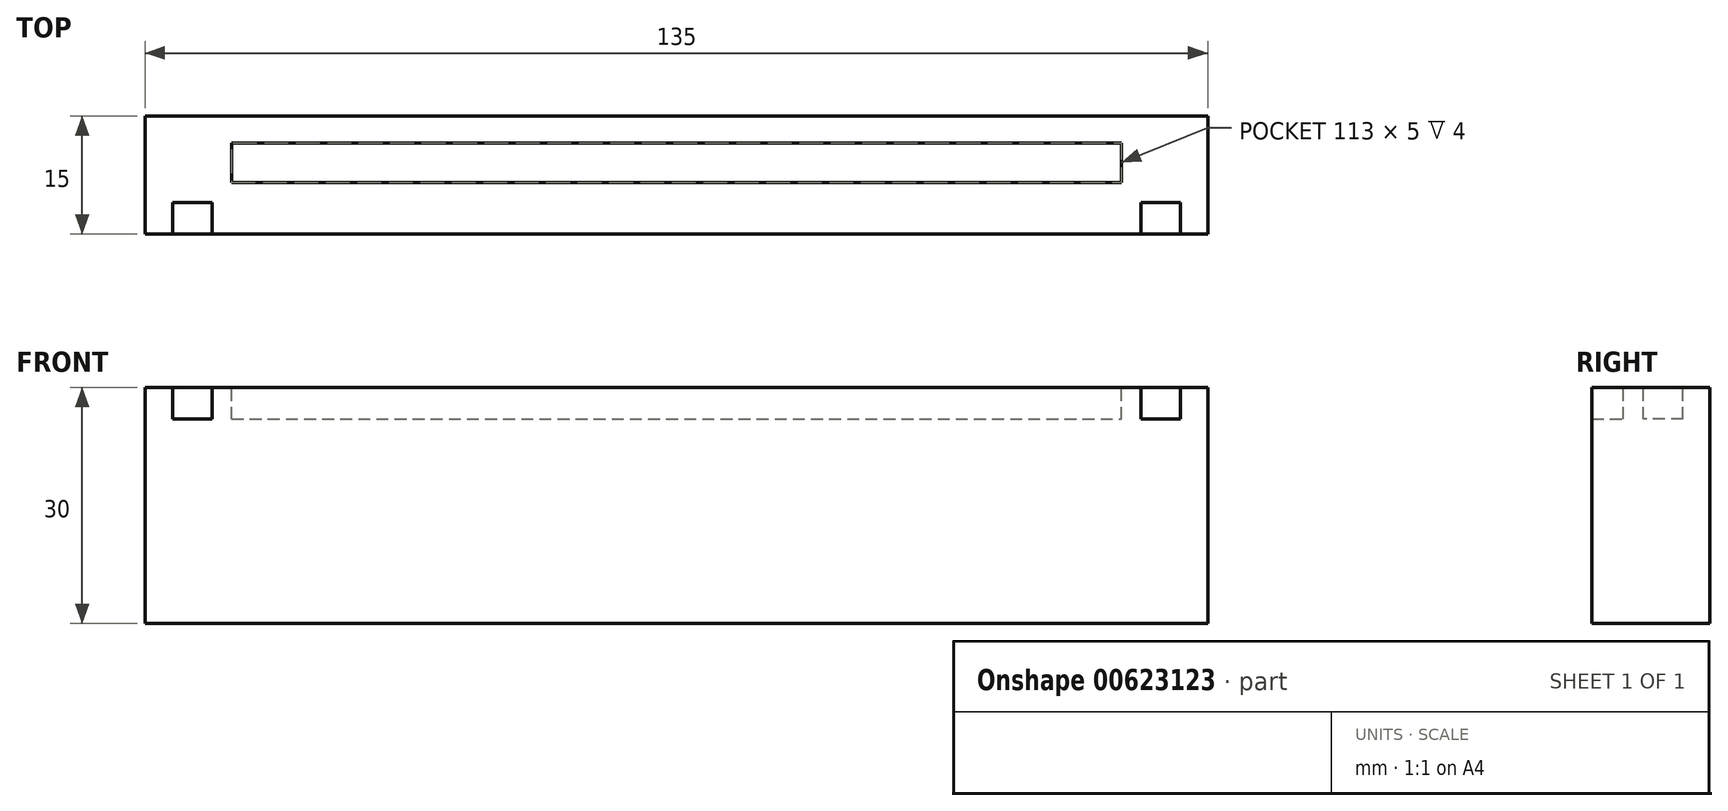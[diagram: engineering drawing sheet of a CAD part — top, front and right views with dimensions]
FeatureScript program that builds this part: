
annotation { "Feature Type Name" : "Feature", "Feature Type Description" : "" }
export const myFeature = defineFeature(function(context is Context, id is Id, definition is map)
    precondition{}
    {
        {
            var Q0;
            Q0=qCreatedBy(makeId("Front.planeOp"),FACE);
            var sketch = newSketch(context, id + "F0", { "sketchPlane" : qUnion([Q0])});
            skLineSegment(sketch, "E0.bottom", {"start": v(-67.5, 0) * mm, "end": v(67.5, 0) * mm});
            skLineSegment(sketch, "E0.top", {"start": v(-67.5, 30) * mm, "end": v(67.5, 30) * mm});
            skLineSegment(sketch, "E0.left", {"start": v(-67.5, 0) * mm, "end": v(-67.5, 30) * mm});
            skLineSegment(sketch, "E0.right", {"start": v(67.5, 0) * mm, "end": v(67.5, 30) * mm});
            skSolve(sketch);
        }
        {
            var Q0;
            Q0 = qSketchRegion(id + "F0", true);
            extrude(context, id + "F1", {"entities" : qUnion([Q0]), "depth" : 15 * mm, "offsetDistance" : 25 * mm});
        }
        {
            var Q0;
            Q0=makeQuery(id+"F1.opExtrude","SWEPT_FACE",FACE,{"disambiguationData":[OSD([sQuery(id+"F0.wireOp",EDGE,"E0.top")])]});
            var sketch = newSketch(context, id + "F2", { "sketchPlane" : qUnion([Q0])});
            skLineSegment(sketch, "E1.bottom", {"start": v(-56.5, -3.45) * mm, "end": v(56.5, -3.45) * mm});
            skLineSegment(sketch, "E1.top", {"start": v(-56.5, -8.45) * mm, "end": v(56.5, -8.45) * mm});
            skLineSegment(sketch, "E1.left", {"start": v(-56.5, -3.45) * mm, "end": v(-56.5, -8.45) * mm});
            skLineSegment(sketch, "E1.right", {"start": v(56.5, -3.45) * mm, "end": v(56.5, -8.45) * mm});
            skLineSegment(sketch, "E2", {"start": v(0, 16.32) * mm, "end": v(0, -25.4) * mm, "construction": true});
            skSolve(sketch);
        }
        {
            var Q0;
            Q0=makeQuery(id+"F2.imprint","IMPRINT",FACE,{"disambiguationData":[TD([[makeQuery(id+"F2.imprint","IMPRINT",EDGE,{"derivedFrom":sQuery(id+"F2.wireOp",EDGE,"E1.bottom")}),-1.0]])]});
            extrude(context, id + "F3", {"entities" : qUnion([Q0]), "operationType" : NewBodyOperationType.REMOVE, "oppositeDirection" : true, "depth" : 4 * mm, "offsetDistance" : 25 * mm});
        }
        {
            var Q0;
            Q0=makeQuery(id+"F1.opExtrude","SWEPT_FACE",FACE,{"disambiguationData":[OSD([sQuery(id+"F0.wireOp",EDGE,"E0.top")])]});
            var sketch = newSketch(context, id + "F4", { "sketchPlane" : qUnion([Q0])});
            skLineSegment(sketch, "E3.bottom", {"start": v(59, -15) * mm, "end": v(64, -15) * mm});
            skLineSegment(sketch, "E3.top", {"start": v(59, -11) * mm, "end": v(64, -11) * mm});
            skLineSegment(sketch, "E3.left", {"start": v(59, -15) * mm, "end": v(59, -11) * mm});
            skLineSegment(sketch, "E3.right", {"start": v(64, -15) * mm, "end": v(64, -11) * mm});
            skLineSegment(sketch, "E4.MirrorCS", {"start": v(-59, -15) * mm, "end": v(-64, -15) * mm});
            skLineSegment(sketch, "E5.MirrorCS", {"start": v(-59, -15) * mm, "end": v(-59, -11) * mm});
            skLineSegment(sketch, "E6.MirrorCS", {"start": v(-59, -11) * mm, "end": v(-64, -11) * mm});
            skLineSegment(sketch, "E7.MirrorCS", {"start": v(-64, -15) * mm, "end": v(-64, -11) * mm});
            skSolve(sketch);
        }
        {
            var Q0;
            Q0=makeQuery(id+"F4.imprint","IMPRINT",FACE,{"disambiguationData":[TD([[makeQuery(id+"F4.imprint","IMPRINT",EDGE,{"derivedFrom":sQuery(id+"F4.wireOp",EDGE,"E3.bottom")}),1.0]])]});
            var Q1;
            Q1=makeQuery(id+"F4.imprint","IMPRINT",FACE,{"disambiguationData":[TD([[makeQuery(id+"F4.imprint","IMPRINT",EDGE,{"derivedFrom":sQuery(id+"F4.wireOp",EDGE,"E4.MirrorCS")}),1.0]])]});
            extrude(context, id + "F5", {"entities" : qUnion([Q0, Q1]), "operationType" : NewBodyOperationType.REMOVE, "oppositeDirection" : true, "depth" : 4 * mm, "offsetDistance" : 25 * mm});
        }
    });
